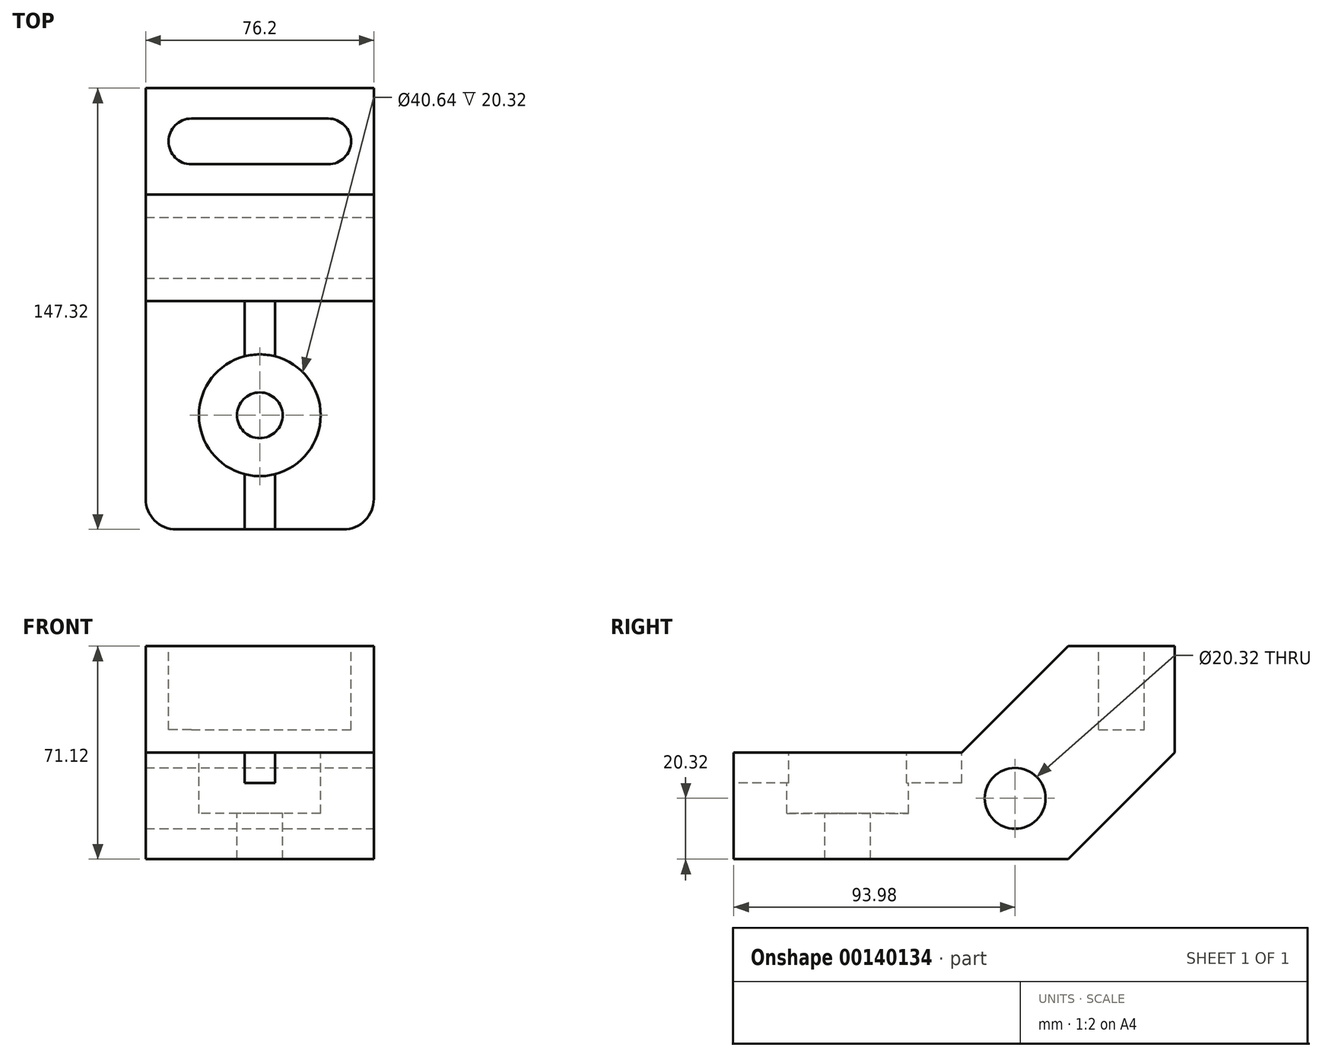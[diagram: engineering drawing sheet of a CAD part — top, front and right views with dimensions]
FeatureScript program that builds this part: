
annotation { "Feature Type Name" : "Feature", "Feature Type Description" : "" }
export const myFeature = defineFeature(function(context is Context, id is Id, definition is map)
    precondition{}
    {
        {
            var Q0;
            Q0=qCreatedBy(makeId("Right.planeOp"),FACE);
            var sketch = newSketch(context, id + "F0", { "sketchPlane" : qUnion([Q0])});
            skLineSegment(sketch, "E0", {"start": v(-111.76, 35.56) * mm, "end": v(-111.76, 0) * mm});
            skLineSegment(sketch, "E1", {"start": v(-111.76, 0) * mm, "end": v(0, 0) * mm});
            skLineSegment(sketch, "E2", {"start": v(-111.76, 35.56) * mm, "end": v(-35.56, 35.56) * mm});
            skLineSegment(sketch, "E3", {"start": v(0, 0) * mm, "end": v(35.56, 35.56) * mm});
            skLineSegment(sketch, "E4", {"start": v(35.56, 35.56) * mm, "end": v(35.56, 71.12) * mm});
            skLineSegment(sketch, "E5", {"start": v(35.56, 71.12) * mm, "end": v(0, 71.12) * mm});
            skLineSegment(sketch, "E6", {"start": v(0, 71.12) * mm, "end": v(-35.56, 35.56) * mm});
            skSolve(sketch);
        }
        {
            var Q0;
            Q0 = qSketchRegion(id + "F0", true);
            extrude(context, id + "F1", {"entities" : qUnion([Q0]), "depth" : 76.2 * mm});
        }
        {
            var Q0;
            Q0=makeQuery(id+"F1.opExtrude","SWEPT_FACE",FACE,{"disambiguationData":[OSD([sQuery(id+"F0.wireOp",EDGE,"E2")])]});
            var sketch = newSketch(context, id + "F2", { "sketchPlane" : qUnion([Q0])});
            skLineSegment(sketch, "E7.bottom", {"start": v(33.02, -35.56) * mm, "end": v(43.18, -35.56) * mm});
            skLineSegment(sketch, "E7.top", {"start": v(33.02, -111.76) * mm, "end": v(43.18, -111.76) * mm});
            skLineSegment(sketch, "E7.left", {"start": v(33.02, -35.56) * mm, "end": v(33.02, -111.76) * mm});
            skLineSegment(sketch, "E7.right", {"start": v(43.18, -35.56) * mm, "end": v(43.18, -111.76) * mm});
            skSolve(sketch);
        }
        {
            var Q0;
            Q0 = qSketchRegion(id + "F2", true);
            extrude(context, id + "F3", {"entities" : qUnion([Q0]), "operationType" : NewBodyOperationType.REMOVE, "oppositeDirection" : true, "depth" : 10.16 * mm});
        }
        {
            var Q0;
            Q0=makeQuery(id+"F1.opExtrude","SWEPT_FACE",FACE,{"disambiguationData":[OSD([sQuery(id+"F0.wireOp",EDGE,"E5")])]});
            var sketch = newSketch(context, id + "F4", { "sketchPlane" : qUnion([Q0])});
            skLineSegment(sketch, "E8", {"start": v(15.24, 25.4) * mm, "end": v(60.96, 25.4) * mm});
            skLineSegment(sketch, "E9", {"start": v(15.24, 10.16) * mm, "end": v(60.96, 10.16) * mm});
            skArc(sketch, "E10", {"start": v(60.96, 10.16) * mm, "mid": v(68.58, 17.78) * mm, "end": v(60.96, 25.4) * mm});
            skArc(sketch, "E11", {"start": v(15.24, 25.4) * mm, "mid": v(7.62, 17.78) * mm, "end": v(15.24, 10.16) * mm});
            skSolve(sketch);
        }
        {
            var Q0;
            Q0 = qSketchRegion(id + "F4", true);
            extrude(context, id + "F5", {"entities" : qUnion([Q0]), "operationType" : NewBodyOperationType.REMOVE, "oppositeDirection" : true, "depth" : 27.94 * mm});
        }
        {
            var Q0;
            {var subQ1=sQuery(id+"F0.wireOp",EDGE,"E2");Q0=makeQuery(id+"F3.boolean.opBoolean","SPLIT",FACE,{"disambiguationData":[TD([makeQuery(id+"F3.opExtrude","SWEPT_FACE",FACE,{"disambiguationData":[OSD([sQuery(id+"F2.wireOp",EDGE,"E7.left")])]})])],"derivedFrom":makeQuery(id+"F1.opExtrude","SWEPT_FACE",FACE,{"disambiguationData":[OSD([subQ1])]})});}
            var sketch = newSketch(context, id + "F6", { "sketchPlane" : qUnion([Q0])});
            skPoint(sketch, "E12", {"position": v(38.1, -73.66) * mm});
            skSolve(sketch);
        }
        {
            var Q0;
            Q0=sQuery(id+"F6.wireOp",VERTEX,"E12");
            var Q1;
            Q1=makeQuery(id+"F1.opExtrude","SWEPT_BODY",BODY,{"disambiguationData":[OSD([sQuery(id+"F0.wireOp",EDGE,"E0"),sQuery(id+"F0.wireOp",EDGE,"E1"),sQuery(id+"F0.wireOp",EDGE,"E2"),sQuery(id+"F0.wireOp",EDGE,"E3"),sQuery(id+"F0.wireOp",EDGE,"E4"),sQuery(id+"F0.wireOp",EDGE,"E5"),sQuery(id+"F0.wireOp",EDGE,"E6")])]});
            hole(context, id + "F7", {"style" : HoleStyle.C_BORE, "endStyle" : HoleEndStyle.THROUGH, "holeDiameter" : 15.24 * mm, "cBoreDiameter" : 40.64 * mm, "cBoreDepth" : 10.16 * mm, "locations" : qUnion([Q0]), "scope" : qUnion([Q1]), "isTappedThrough" : true});
        }
        {
            var Q0;
            Q0=makeQuery(id+"F1.opExtrude","CAP_FACE",FACE,{"disambiguationData":[OSD([sQuery(id+"F0.wireOp",EDGE,"E0"),sQuery(id+"F0.wireOp",EDGE,"E1"),sQuery(id+"F0.wireOp",EDGE,"E2"),sQuery(id+"F0.wireOp",EDGE,"E3"),sQuery(id+"F0.wireOp",EDGE,"E4"),sQuery(id+"F0.wireOp",EDGE,"E5"),sQuery(id+"F0.wireOp",EDGE,"E6")])],"isStart":false});
            var sketch = newSketch(context, id + "F8", { "sketchPlane" : qUnion([Q0])});
            skPoint(sketch, "E13", {"position": v(-17.78, 20.32) * mm});
            skSolve(sketch);
        }
        {
            var Q0;
            Q0=sQuery(id+"F8.wireOp",VERTEX,"E13");
            var Q1;
            Q1=makeQuery(id+"F1.opExtrude","SWEPT_BODY",BODY,{"disambiguationData":[OSD([sQuery(id+"F0.wireOp",EDGE,"E0"),sQuery(id+"F0.wireOp",EDGE,"E1"),sQuery(id+"F0.wireOp",EDGE,"E2"),sQuery(id+"F0.wireOp",EDGE,"E3"),sQuery(id+"F0.wireOp",EDGE,"E4"),sQuery(id+"F0.wireOp",EDGE,"E5"),sQuery(id+"F0.wireOp",EDGE,"E6")])]});
            hole(context, id + "F9", {"style" : HoleStyle.SIMPLE, "endStyle" : HoleEndStyle.THROUGH, "holeDiameter" : 20.32 * mm, "locations" : qUnion([Q0]), "scope" : qUnion([Q1]), "isTappedThrough" : true});
        }
        {
            var Q0;
            Q0=makeQuery(id+"F1.opExtrude","CAP_EDGE",EDGE,{"disambiguationData":[OSD([sQuery(id+"F0.wireOp",EDGE,"E0")])],"isStart":true});
            var Q1;
            Q1=makeQuery(id+"F1.opExtrude","CAP_EDGE",EDGE,{"disambiguationData":[OSD([sQuery(id+"F0.wireOp",EDGE,"E0")])],"isStart":false});
            fillet(context, id + "F10", {"entities" : qUnion([Q0, Q1]), "radius" : 10.16 * mm, "tangentPropagation" : true, "allowEdgeOverflow" : false});
        }
    });
